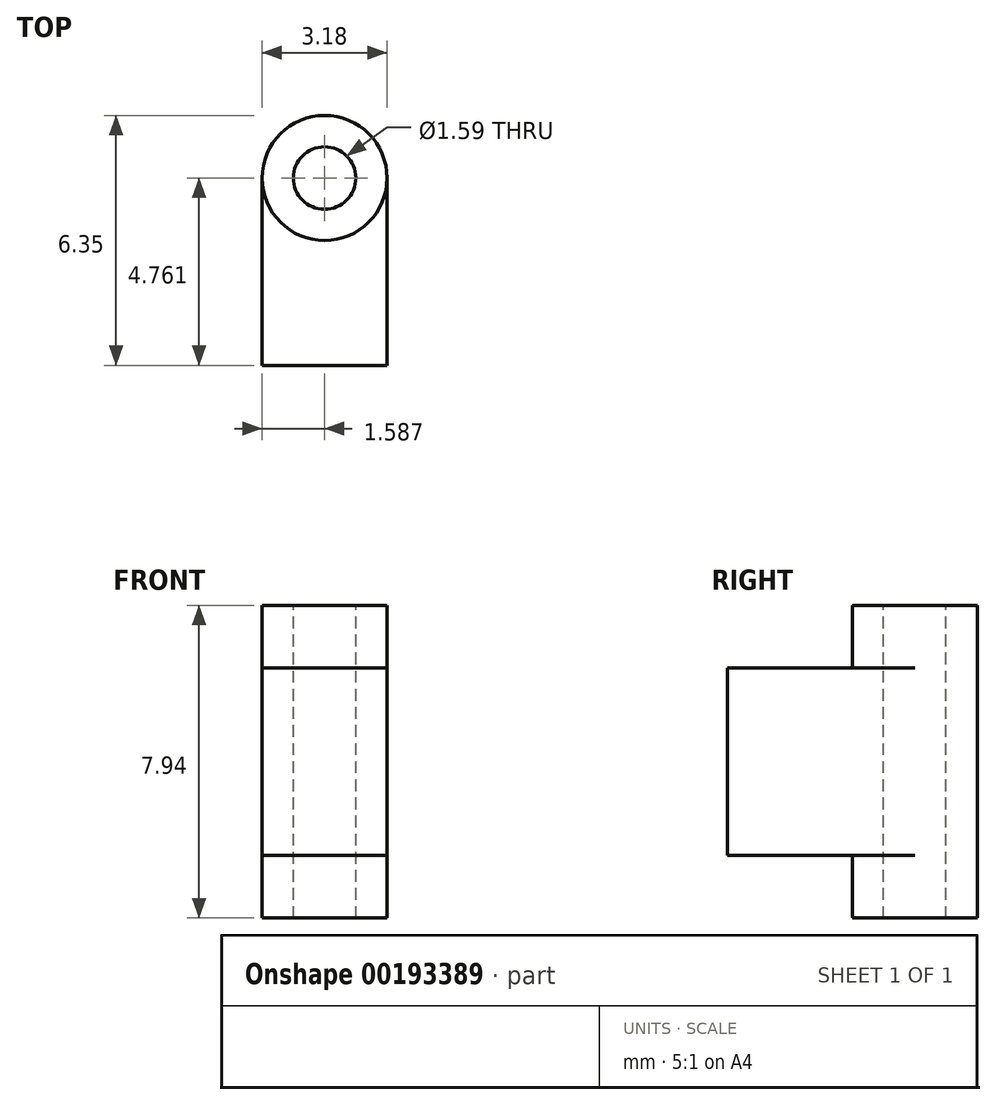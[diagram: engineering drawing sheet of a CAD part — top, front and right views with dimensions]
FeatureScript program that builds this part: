
annotation { "Feature Type Name" : "Feature", "Feature Type Description" : "" }
export const myFeature = defineFeature(function(context is Context, id is Id, definition is map)
    precondition{}
    {
        {
            var Q0;
            Q0=qCreatedBy(makeId("Right.planeOp"),FACE);
            var sketch = newSketch(context, id + "F0", { "sketchPlane" : qUnion([Q0])});
            skLineSegment(sketch, "E0.bottom", {"start": v(2.38, 2.38) * mm, "end": v(-2.38, 2.38) * mm});
            skLineSegment(sketch, "E0.top", {"start": v(2.38, -2.38) * mm, "end": v(-2.38, -2.38) * mm});
            skLineSegment(sketch, "E0.left", {"start": v(2.38, 2.38) * mm, "end": v(2.38, -2.38) * mm});
            skLineSegment(sketch, "E0.right", {"start": v(-2.38, 2.38) * mm, "end": v(-2.38, -2.38) * mm});
            skPoint(sketch, "E0.middle", {"position": v(0, 0) * mm});
            skSolve(sketch);
        }
        {
            var Q0;
            Q0=makeQuery(id+"F0.imprint","IMPRINT",FACE,{"disambiguationData":[TD([[makeQuery(id+"F0.imprint","IMPRINT",EDGE,{"derivedFrom":sQuery(id+"F0.wireOp",EDGE,"E0.bottom")}),1.0]])]});
            extrude(context, id + "F1", {"entities" : qUnion([Q0]), "depth" : 3.17 * mm});
        }
        {
            var Q0;
            Q0=makeQuery(id+"F1.opExtrude","SWEPT_FACE",FACE,{"disambiguationData":[OSD([sQuery(id+"F0.wireOp",EDGE,"E0.bottom")])]});
            var sketch = newSketch(context, id + "F2", { "sketchPlane" : qUnion([Q0])});
            skCircle(sketch, "E1", {"center": v(1.59, 2.38) * mm, "radius": 1.59 * mm});
            skPoint(sketch, "E2", {"position": v(1.59, 3.97) * mm});
            skSolve(sketch);
        }
        {
            var Q0;
            Q0 = qSketchRegion(id + "F2", true);
            extrude(context, id + "F3", {"entities" : qUnion([Q0]), "operationType" : NewBodyOperationType.ADD, "oppositeDirection" : true, "depth" : 6.35 * mm});
        }
        {
            var Q0;
            Q0 = qSketchRegion(id + "F2", true);
            extrude(context, id + "F4", {"entities" : qUnion([Q0]), "operationType" : NewBodyOperationType.ADD, "depth" : 1.59 * mm});
        }
        {
            var Q0;
            Q0=makeQuery(id+"F4.opExtrude","CAP_FACE",FACE,{"disambiguationData":[OSD([sQuery(id+"F2.wireOp",EDGE,"E1")])],"isStart":false});
            var sketch = newSketch(context, id + "F5", { "sketchPlane" : qUnion([Q0])});
            skCircle(sketch, "E3", {"center": v(1.59, 2.38) * mm, "radius": 0.8 * mm});
            skSolve(sketch);
        }
        {
            var Q0;
            Q0=makeQuery(id+"F5.imprint","IMPRINT",FACE,{"disambiguationData":[TD([[makeQuery(id+"F5.imprint","IMPRINT",EDGE,{"derivedFrom":sQuery(id+"F5.wireOp",EDGE,"E3")}),1.0]])]});
            extrude(context, id + "F6", {"entities" : qUnion([Q0]), "operationType" : NewBodyOperationType.REMOVE, "endBound" : BoundingType.THROUGH_ALL, "oppositeDirection" : true, "depth" : 25.4 * mm});
        }
    });
